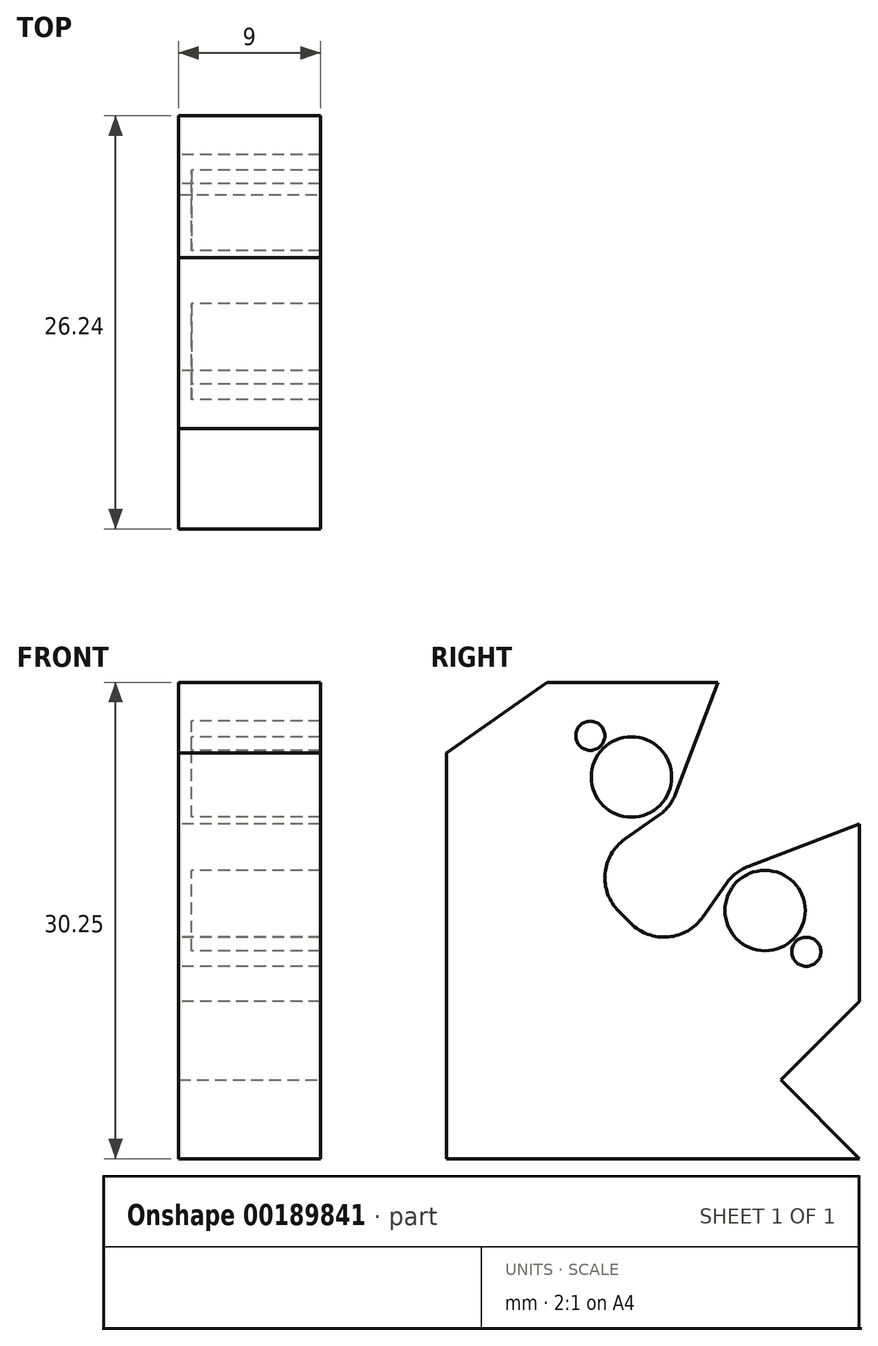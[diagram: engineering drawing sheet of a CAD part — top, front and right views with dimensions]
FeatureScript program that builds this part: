
annotation { "Feature Type Name" : "Feature", "Feature Type Description" : "" }
export const myFeature = defineFeature(function(context is Context, id is Id, definition is map)
    precondition{}
    {
        {
            var Q0;
            Q0=qCreatedBy(makeId("Right.planeOp"),FACE);
            var sketch = newSketch(context, id + "F0", { "sketchPlane" : qUnion([Q0])});
            skCircle(sketch, "E0", {"center": v(-24.24, 8.49) * mm, "radius": 2.55 * mm});
            skCircle(sketch, "E1", {"center": v(-15.76, 0) * mm, "radius": 2.55 * mm});
            skLineSegment(sketch, "E2", {"start": v(0, 0) * mm, "end": v(0, 30.5) * mm, "construction": true});
            skLineSegment(sketch, "E3", {"start": v(-24.24, 8.49) * mm, "end": v(-15.76, 0) * mm, "construction": true});
            skPoint(sketch, "E4", {"position": v(-20, 4.24) * mm});
            skLineSegment(sketch, "E5", {"start": v(-20, 4.24) * mm, "end": v(-20, -15.06) * mm, "construction": true});
            skCircle(sketch, "E6.0", {"center": v(-24.24, 8.49) * mm, "radius": 3 * mm});
            skCircle(sketch, "E7.0", {"center": v(-15.76, 0) * mm, "radius": 3 * mm});
            skLineSegment(sketch, "E8", {"start": v(-24.65, 4.54) * mm, "end": v(-22.52, 6.03) * mm});
            skLineSegment(sketch, "E9", {"start": v(-21.44, 7.42) * mm, "end": v(-18.75, 14.49) * mm});
            skLineSegment(sketch, "E10", {"start": v(-18.75, 14.49) * mm, "end": v(-29.62, 14.49) * mm});
            skLineSegment(sketch, "E11", {"start": v(-29.62, 14.49) * mm, "end": v(-36, 10.02) * mm});
            skLineSegment(sketch, "E12", {"start": v(-36, 10.02) * mm, "end": v(-36, -5.76) * mm});
            skLineSegment(sketch, "E13", {"start": v(-36, -5.76) * mm, "end": v(-20, -5.76) * mm});
            skLineSegment(sketch, "E14", {"start": v(-20, 4.24) * mm, "end": v(-11.7, 12.54) * mm, "construction": true});
            skLineSegment(sketch, "E15.MirrorCS", {"start": v(-16.82, 2.8) * mm, "end": v(-9.76, 5.49) * mm});
            skLineSegment(sketch, "E16.MirrorCS", {"start": v(-9.76, 5.49) * mm, "end": v(-9.76, -5.38) * mm});
            skLineSegment(sketch, "E17.MirrorCS", {"start": v(-19.7, -0.4) * mm, "end": v(-18.21, 1.72) * mm});
            skLineSegment(sketch, "E18", {"start": v(-25.05, -0.04) * mm, "end": v(-24.29, -0.81) * mm});
            skLineSegment(sketch, "E19", {"start": v(-20, -5.76) * mm, "end": v(-9.76, -5.76) * mm});
            skLineSegment(sketch, "E20", {"start": v(-9.76, -5.76) * mm, "end": v(-9.76, -5.38) * mm});
            skPoint(sketch, "E21.visualSharp", {"position": v(-27.58, 2.49) * mm});
            skArc(sketch, "E21.filletArc", {"start": v(-24.65, 4.54) * mm, "mid": v(-25.92, 2.34) * mm, "end": v(-25.05, -0.04) * mm});
            skPoint(sketch, "E22.visualSharp", {"position": v(-21.76, -3.34) * mm});
            skArc(sketch, "E22.filletArc", {"start": v(-24.29, -0.81) * mm, "mid": v(-21.9, -1.68) * mm, "end": v(-19.7, -0.4) * mm});
            skLineSegment(sketch, "E23", {"start": v(-24.24, 8.49) * mm, "end": v(-26.86, 11.1) * mm, "construction": true});
            skCircle(sketch, "E24", {"center": v(-26.86, 11.1) * mm, "radius": 0.93 * mm});
            skCircle(sketch, "E25.MirrorC", {"center": v(-13.14, -2.62) * mm, "radius": 0.93 * mm});
            skSolve(sketch);
        }
        {
            var Q0;
            Q0 = qSketchRegion(id + "F0", true);
            extrude(context, id + "F1", {"entities" : qUnion([Q0]), "depth" : 9 * mm});
        }
        {
            var Q0;
            Q0=makeQuery(id+"F0.imprint","IMPRINT",FACE,{"disambiguationData":[TD([[makeQuery(id+"F0.imprint","IMPRINT",EDGE,{"derivedFrom":sQuery(id+"F0.wireOp",EDGE,"E1")}),1.0]])]});
            var Q1;
            Q1=makeQuery(id+"F0.imprint","IMPRINT",FACE,{"disambiguationData":[TD([[makeQuery(id+"F0.imprint","IMPRINT",EDGE,{"derivedFrom":sQuery(id+"F0.wireOp",EDGE,"E0")}),1.0]])]});
            var Q2;
            Q2=makeQuery(id+"F0.imprint","IMPRINT",FACE,{"disambiguationData":[TD([[makeQuery(id+"F0.imprint","IMPRINT",EDGE,{"derivedFrom":sQuery(id+"F0.wireOp",EDGE,"E24")}),1.0]])]});
            var Q3;
            Q3=makeQuery(id+"F0.imprint","IMPRINT",FACE,{"disambiguationData":[TD([[makeQuery(id+"F0.imprint","IMPRINT",EDGE,{"derivedFrom":sQuery(id+"F0.wireOp",EDGE,"E25.MirrorC")}),-1.0]])]});
            extrude(context, id + "F2", {"entities" : qUnion([Q0, Q1, Q2, Q3]), "operationType" : NewBodyOperationType.ADD, "depth" : 0.8 * mm});
        }
        {
            var Q0;
            {var subQ0=sQuery(id+"F0.wireOp",EDGE,"E8");Q0=makeQuery(id+"F0.imprint","IMPRINT",FACE,{"disambiguationData":[TD([[makeQuery(id+"F0.imprint","IMPRINT",EDGE,{"derivedFrom":subQ0}),1.0]])]});}
            var sketch = newSketch(context, id + "F3", { "sketchPlane" : qUnion([Q0])});
            skLineSegment(sketch, "E26.0", {"start": v(-36, 10.02) * mm, "end": v(-36, -5.76) * mm});
            skLineSegment(sketch, "E27.0", {"start": v(-36, -5.76) * mm, "end": v(-20, -5.76) * mm});
            skLineSegment(sketch, "E28.0", {"start": v(-20, -5.76) * mm, "end": v(-9.76, -5.76) * mm});
            skPoint(sketch, "E29.0", {"position": v(-20, 4.24) * mm});
            skLineSegment(sketch, "E30", {"start": v(-20, 4.24) * mm, "end": v(-20, -15.76) * mm, "construction": true});
            skLineSegment(sketch, "E31", {"start": v(-9.76, -5.76) * mm, "end": v(-19.76, -15.76) * mm});
            skLineSegment(sketch, "E32", {"start": v(-36, -5.76) * mm, "end": v(-36, -15.76) * mm});
            skLineSegment(sketch, "E33", {"start": v(-36, -15.76) * mm, "end": v(-19.76, -15.76) * mm});
            skSolve(sketch);
        }
        {
            var Q0;
            Q0=makeQuery(id+"F3.imprint","IMPRINT",FACE,{"disambiguationData":[TD([[makeQuery(id+"F3.imprint","IMPRINT",EDGE,{"derivedFrom":sQuery(id+"F3.wireOp",EDGE,"E27.0")}),-1.0]])]});
            var Q1;
            Q1=makeQuery(id+"F1.opExtrude","CAP_FACE",FACE,{"disambiguationData":[OSD([sQuery(id+"F0.wireOp",EDGE,"E0"),sQuery(id+"F0.wireOp",EDGE,"E1"),sQuery(id+"F0.wireOp",EDGE,"E6.0"),sQuery(id+"F0.wireOp",EDGE,"E7.0"),sQuery(id+"F0.wireOp",EDGE,"E8"),sQuery(id+"F0.wireOp",EDGE,"E9"),sQuery(id+"F0.wireOp",EDGE,"E10"),sQuery(id+"F0.wireOp",EDGE,"E11"),sQuery(id+"F0.wireOp",EDGE,"E12"),sQuery(id+"F0.wireOp",EDGE,"E13"),sQuery(id+"F0.wireOp",EDGE,"E15.MirrorCS"),sQuery(id+"F0.wireOp",EDGE,"E16.MirrorCS"),sQuery(id+"F0.wireOp",EDGE,"E17.MirrorCS"),sQuery(id+"F0.wireOp",EDGE,"E18"),sQuery(id+"F0.wireOp",EDGE,"E19"),sQuery(id+"F0.wireOp",EDGE,"E20"),sQuery(id+"F0.wireOp",EDGE,"E21.filletArc"),sQuery(id+"F0.wireOp",EDGE,"E22.filletArc")])],"isStart":false});
            extrude(context, id + "F4", {"entities" : qUnion([Q0]), "operationType" : NewBodyOperationType.ADD, "endBound" : BoundingType.UP_TO_SURFACE, "endBoundEntityFace" : qUnion([Q1]), "depth" : 25 * mm});
        }
        {
            var Q0;
            {var subQ0=sQuery(id+"F0.wireOp",EDGE,"E25.MirrorC");var subQ1=sQuery(id+"F0.wireOp",EDGE,"E24");var subQ2=sQuery(id+"F0.wireOp",EDGE,"E22.filletArc");var subQ3=sQuery(id+"F0.wireOp",EDGE,"E21.filletArc");var subQ4=sQuery(id+"F0.wireOp",EDGE,"E20");var subQ5=sQuery(id+"F0.wireOp",EDGE,"E19");var subQ6=sQuery(id+"F0.wireOp",EDGE,"E18");var subQ7=sQuery(id+"F0.wireOp",EDGE,"E17.MirrorCS");var subQ8=sQuery(id+"F0.wireOp",EDGE,"E16.MirrorCS");var subQ9=sQuery(id+"F0.wireOp",EDGE,"E15.MirrorCS");var subQ10=sQuery(id+"F0.wireOp",EDGE,"E13");var subQ11=sQuery(id+"F0.wireOp",EDGE,"E12");var subQ12=sQuery(id+"F0.wireOp",EDGE,"E11");var subQ13=sQuery(id+"F0.wireOp",EDGE,"E10");var subQ14=sQuery(id+"F0.wireOp",EDGE,"E9");var subQ15=sQuery(id+"F0.wireOp",EDGE,"E8");var subQ16=sQuery(id+"F0.wireOp",EDGE,"E7.0");var subQ17=sQuery(id+"F0.wireOp",EDGE,"E6.0");var subQ18=sQuery(id+"F0.wireOp",EDGE,"E1");var subQ19=sQuery(id+"F0.wireOp",EDGE,"E0");Q0=makeQuery(id+"F4.boolean.opBoolean","MERGE",FACE,{"derivedFrom":[makeQuery(id+"F1.opExtrude","CAP_FACE",FACE,{"disambiguationData":[OSD([subQ19,subQ18,subQ17,subQ16,subQ15,subQ14,subQ13,subQ12,subQ11,subQ10,subQ9,subQ8,subQ7,subQ6,subQ5,subQ4,subQ3,subQ2,subQ1,subQ0])],"isStart":false}),makeQuery(id+"F4.opExtrude","CAP_FACE",FACE,{"disambiguationData":[OSD([subQ19,subQ18,subQ17,subQ16,subQ15,subQ14,subQ13,subQ12,subQ11,subQ10,subQ9,subQ8,subQ7,subQ6,subQ5,subQ4,subQ3,subQ2,subQ1,subQ0])],"isStart":false})]});}
            var sketch = newSketch(context, id + "F5", { "sketchPlane" : qUnion([Q0])});
            skLineSegment(sketch, "E34.0", {"start": v(-24.24, 8.49) * mm, "end": v(-15.76, 0) * mm});
            skCircle(sketch, "E35.0", {"center": v(-24.24, 8.49) * mm, "radius": 3 * mm});
            skCircle(sketch, "E36.0", {"center": v(-15.76, 0) * mm, "radius": 3 * mm});
            skPoint(sketch, "E37", {"position": v(-22.12, 6.36) * mm});
            skPoint(sketch, "E38", {"position": v(-17.88, 2.12) * mm});
            skSolve(sketch);
        }
        {
            var Q0;
            {var subQ13=sQuery(id+"F0.wireOp",EDGE,"E8");var subQ24=makeQuery(id+"F1.opExtrude","CAP_EDGE",EDGE,{"disambiguationData":[OSD([subQ13])],"isStart":false});Q0=makeQuery(id+"F5.imprint","IMPRINT",FACE,{"disambiguationData":[TD([[makeQuery(id+"F5.imprint","IMPRINT",EDGE,{"derivedFrom":subQ24}),1.0]])]});}
            var sketch = newSketch(context, id + "F6", { "sketchPlane" : qUnion([Q0])});
            skLineSegment(sketch, "E39.0", {"start": v(-9.76, -5.76) * mm, "end": v(-19.76, -15.76) * mm});
            skLineSegment(sketch, "E40", {"start": v(-14.76, -10.76) * mm, "end": v(-9.76, -15.76) * mm});
            skLineSegment(sketch, "E41", {"start": v(-9.76, -15.76) * mm, "end": v(-19.76, -15.76) * mm});
            skSolve(sketch);
        }
        {
            var Q0;
            {var subQ2=sQuery(id+"F6.wireOp",EDGE,"E40");Q0=makeQuery(id+"F6.imprint","IMPRINT",FACE,{"disambiguationData":[TD([[makeQuery(id+"F6.imprint","IMPRINT",EDGE,{"derivedFrom":subQ2}),-1.0]])]});}
            var Q1;
            {var subQ0=sQuery(id+"F0.wireOp",EDGE,"E25.MirrorC");var subQ1=sQuery(id+"F0.wireOp",EDGE,"E24");var subQ2=sQuery(id+"F0.wireOp",EDGE,"E1");var subQ3=sQuery(id+"F0.wireOp",EDGE,"E0");Q1=makeQuery(id+"F4.boolean.opBoolean","MERGE",FACE,{"derivedFrom":[makeQuery(id+"F2.boolean.opBoolean","MERGE",FACE,{"derivedFrom":[makeQuery(id+"F1.opExtrude","CAP_FACE",FACE,{"disambiguationData":[OSD([subQ3,subQ2,sQuery(id+"F0.wireOp",EDGE,"E6.0"),sQuery(id+"F0.wireOp",EDGE,"E7.0"),sQuery(id+"F0.wireOp",EDGE,"E8"),sQuery(id+"F0.wireOp",EDGE,"E9"),sQuery(id+"F0.wireOp",EDGE,"E10"),sQuery(id+"F0.wireOp",EDGE,"E11"),sQuery(id+"F0.wireOp",EDGE,"E12"),sQuery(id+"F0.wireOp",EDGE,"E13"),sQuery(id+"F0.wireOp",EDGE,"E15.MirrorCS"),sQuery(id+"F0.wireOp",EDGE,"E16.MirrorCS"),sQuery(id+"F0.wireOp",EDGE,"E17.MirrorCS"),sQuery(id+"F0.wireOp",EDGE,"E18"),sQuery(id+"F0.wireOp",EDGE,"E19"),sQuery(id+"F0.wireOp",EDGE,"E20"),sQuery(id+"F0.wireOp",EDGE,"E21.filletArc"),sQuery(id+"F0.wireOp",EDGE,"E22.filletArc"),subQ1,subQ0])],"isStart":true}),makeQuery(id+"F2.opExtrude","CAP_FACE",FACE,{"disambiguationData":[OSD([subQ3])],"isStart":true}),makeQuery(id+"F2.opExtrude","CAP_FACE",FACE,{"disambiguationData":[OSD([subQ2])],"isStart":true}),makeQuery(id+"F2.opExtrude","CAP_FACE",FACE,{"disambiguationData":[OSD([subQ1])],"isStart":true}),makeQuery(id+"F2.opExtrude","CAP_FACE",FACE,{"disambiguationData":[OSD([subQ0])],"isStart":true})]}),makeQuery(id+"F4.opExtrude","CAP_FACE",FACE,{"disambiguationData":[OSD([sQuery(id+"F3.wireOp",EDGE,"E27.0"),sQuery(id+"F3.wireOp",EDGE,"E28.0"),sQuery(id+"F3.wireOp",EDGE,"E31"),sQuery(id+"F3.wireOp",EDGE,"E32"),sQuery(id+"F3.wireOp",EDGE,"E33")])],"isStart":true})]});}
            extrude(context, id + "F7", {"entities" : qUnion([Q0]), "operationType" : NewBodyOperationType.ADD, "endBound" : BoundingType.UP_TO_SURFACE, "oppositeDirection" : true, "endBoundEntityFace" : qUnion([Q1]), "depth" : 25 * mm});
        }
    });
